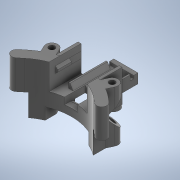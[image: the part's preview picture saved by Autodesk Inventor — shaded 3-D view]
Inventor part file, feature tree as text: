
AUTODESK INVENTOR PART (.ipt)
format: ipt  version: 2020 (Build 240168000, 168)  size: 781,312 bytes
history: native  units: mm
features: extrude x18, sketch x17, projected_geometry x15, other x5, chamfer x2, sweep x1, fillet x1
ambient origin geometry x8: Origin, YZ Plane, XZ Plane, XY Plane, X Axis, Y Axis, Z Axis, Center Point
bodies: Body1 (feature_tree)
feature tree (59):
  other  "Твердое тело1"
  extrude  "Выдавливание1"  Depth=35.0mm TaperAngle=0.0deg
  sketch  "Эскиз2"
  extrude  "Выдавливание2"  Depth=4.0mm
  sweep  "Сдвиг1"
  extrude  "Выдавливание5"  Depth=8.0mm
  extrude  "Выдавливание6"  Depth=35.0mm TaperAngle=0.0deg
  extrude  "Выдавливание7"  Depth=8.5mm
  extrude  "Выдавливание8"  TaperAngle=45.0deg  [1 undecoded]
  other  "РабПлоскость1"
  extrude  "Выдавливание9"  Depth=8.5mm
  extrude  "Выдавливание10"  TaperAngle=45.0deg  [1 undecoded]
  extrude  "Выдавливание11"  TaperAngle=0.0deg  [1 undecoded]
  sketch  "Эскиз13"
  other  "РабПлоскость2"
  sketch  "Эскиз14"
  extrude  "Выдавливание12"  Depth=5.0mm TaperAngle=0.0deg
  extrude  "Выдавливание13"  Depth=15.0mm TaperAngle=0.0deg
  other  "РабПлоскость3"
  extrude  "Выдавливание14"  Depth=15.0mm TaperAngle=0.0deg
  extrude  "Выдавливание15"  Depth=26.0mm
  extrude  "Выдавливание16"  Depth=6.0mm
  extrude  "Выдавливание17"  Depth=15.0mm TaperAngle=0.0deg
  chamfer  "Фаска1"  Distance=2.0mm
  other  "РабПлоскость4"
  sketch  "Эскиз18"
  extrude  "Выдавливание18"  Depth=1.5mm
  extrude  "Выдавливание19"  Depth=3.0mm
  extrude  "Выдавливание20"  Depth=6.0mm
  chamfer  "Фаска2"  Distance=2.5mm
  fillet  "Сопряжение1"  [1 undecoded]
  sketch  "Эскиз1"
  sketch  "Эскиз3"
  projected_geometry  "Спроецированная петля1"
  projected_geometry  "Спроецированная петля2"
  sketch  "3D эскиз1"
  sketch  "Эскиз4"
  sketch  "Эскиз6"
  projected_geometry  "Спроецированная петля4"
  sketch  "Эскиз7"
  projected_geometry  "Спроецированная петля5"
  sketch  "Эскиз9"
  projected_geometry  "Спроецированная петля7"
  sketch  "Эскиз11"
  projected_geometry  "Спроецированная петля8"
  sketch  "Эскиз12"
  projected_geometry  "Спроецированная петля9"
  projected_geometry  "Спроецированная петля10"
  sketch  "Эскиз15"
  sketch  "Эскиз16"
  projected_geometry  "Спроецированная петля11"
  projected_geometry  "Спроецированная петля12"
  sketch  "Эскиз17"
  projected_geometry  "Спроецированная петля13"
  projected_geometry  "Спроецированная петля14"
  projected_geometry  "Спроецированная петля15"
  projected_geometry  "Спроецированная петля16"
  sketch  "Эскиз19"
  projected_geometry  "Спроецированная петля17"
note: 4 required parameter values undecoded (feature->parameter linkage not recoverable at this tier; creation-order binding heuristic only, values carry confidence <= 0.55)
